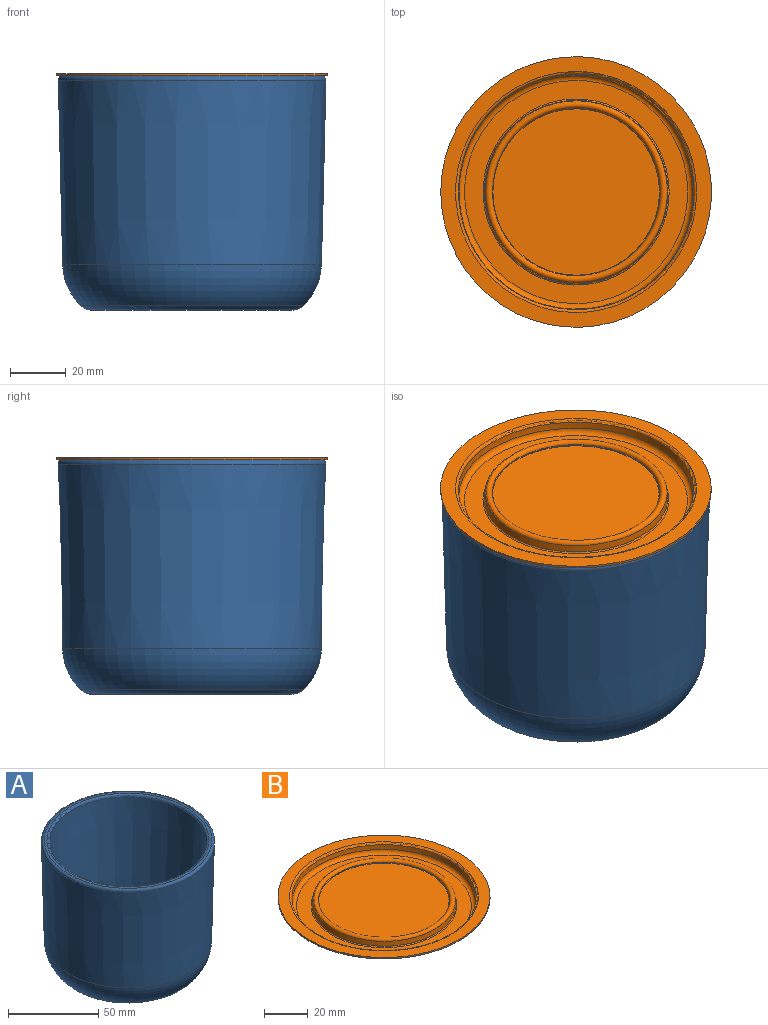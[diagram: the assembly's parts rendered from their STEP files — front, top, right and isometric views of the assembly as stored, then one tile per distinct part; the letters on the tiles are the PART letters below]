
ASSEMBLY  parts=2 mates=1
PART A: 11 faces, bbox 103.8x103.8x88.2 mm
  f0: cone r=43.5mm half-angle=3.5deg, axis (0,0,1), area 18136.1mm2, adj f3,f6
  f1: torus R=35.76mm, axis (0,0,1), area 1107.2mm2, adj f8,f10
  f2: plane 72.35x72.35mm, normal (0,0,1), area 4111.6mm2, adj f3
  f3: torus R=36.18mm, axis (0,0,-1), area 1082.9mm2, adj f0,f2
  f4: torus R=46.46mm, axis (0,0,-1), area 712.8mm2, adj f5,f7
  f5: plane 92.93x92.93mm, normal (0,0,1), area 445.6mm2, adj f4,f6
  f6: torus R=44.91mm, axis (0,0,-1), area 625.9mm2, adj f0,f5
  f7: cone r=46mm half-angle=1.4deg, axis (0,0,1), area 19603.5mm2, adj f4,f9
  f8: cone r=38.2mm half-angle=45.7deg, axis (0,0,1), area 42.3mm2, adj f1,f9
  f9: torus R=25.4mm, axis (0,0,-1), area 4507.6mm2, adj f7,f8
  f10: sphere r=426.91mm, area 4023.6mm2, adj f1
PART B: 22 faces, bbox 97x97x6 mm
  f0: plane 59.63x59.63mm, normal (0,0,-1), area 2793mm2, adj f18
  f1: cone r=30.73mm half-angle=5deg, axis (0,0,1), area 25.4mm2, adj f2,f18
  f2: torus R=31.32mm, axis (0,0,-1), area 292mm2, adj f1,f3
  f3: cone r=31.82mm half-angle=5deg, axis (0,0,-1), area 570.3mm2, adj f2,f17
  f4: plane 79.59x79.59mm, normal (0,0,-1), area 1540.9mm2, adj f15,f17
  f5: cone r=42.55mm half-angle=5deg, axis (0,0,1), area 665.9mm2, adj f6,f15
  f6: plane 97x97mm, normal (0,0,-1), area 1581mm2, adj f5,f7
  f7: cylinder r=48.5mm len=97mm, axis (0,0,-1), area 243.8mm2, adj f6,f8
  f8: plane 97x97mm, normal (0,0,1), area 1531.4mm2, adj f7,f21
  f9: cone r=42.27mm half-angle=5deg, axis (0,0,1), area 653.3mm2, adj f16,f21
  f10: plane 79.96x79.96mm, normal (0,0,1), area 1529.4mm2, adj f16,f20
  f11: cone r=32.88mm half-angle=5deg, axis (0,0,-1), area 527.8mm2, adj f12,f20
  f12: torus R=31.32mm, axis (0,0,-1), area 759.1mm2, adj f11,f13
  f13: cone r=30mm half-angle=5deg, axis (0,0,1), area 24.8mm2, adj f12,f19
  f14: plane 59.63x59.63mm, normal (0,0,1), area 2793mm2, adj f19
  f15: torus R=39.8mm, axis (0,0,-1), area 1164.5mm2, adj f4,f5
  f16: torus R=39.98mm, axis (0,0,1), area 768.3mm2, adj f9,f10
  f17: torus R=33.06mm, axis (0,0,-1), area 302.5mm2, adj f3,f4
  f18: torus R=29.82mm, axis (0,0,-1), area 283.7mm2, adj f0,f1
  f19: torus R=29.82mm, axis (0,0,-1), area 55.8mm2, adj f13,f14
  f20: torus R=33.34mm, axis (0,0,1), area 153.9mm2, adj f10,f11
  f21: torus R=43.18mm, axis (0,0,1), area 396.8mm2, adj f8,f9
PLACE A t=(-7.36,18.17,-8.37)mm
PLACE B t=(-7.36,18.17,70.43)mm
MATE parallel B.f1 <-> A.f0  axis (0,0,-1) through (-7.36,18.17,75.63)mm
